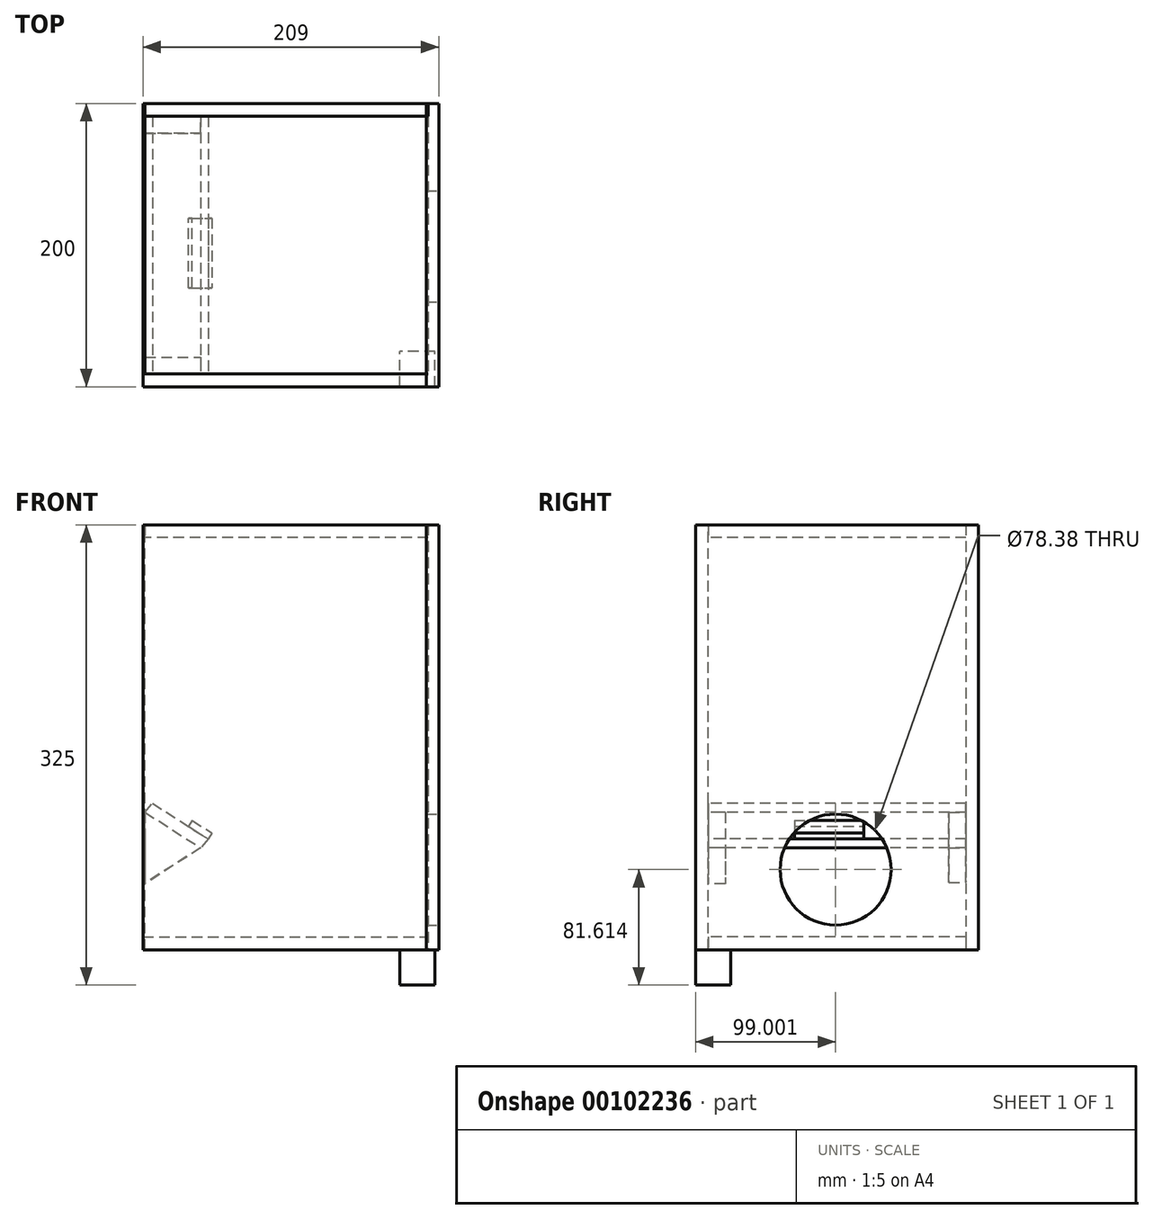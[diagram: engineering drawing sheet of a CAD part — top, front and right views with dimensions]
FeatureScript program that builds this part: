
annotation { "Feature Type Name" : "Feature", "Feature Type Description" : "" }
export const myFeature = defineFeature(function(context is Context, id is Id, definition is map)
    precondition{}
    {
        {
            var Q0;
            Q0=qCreatedBy(makeId("Front.planeOp"),FACE);
            var sketch = newSketch(context, id + "F0", { "sketchPlane" : qUnion([Q0])});
            skLineSegment(sketch, "E0.bottom", {"start": v(0, 0) * mm, "end": v(200, 0) * mm});
            skLineSegment(sketch, "E0.top", {"start": v(0, 300) * mm, "end": v(200, 300) * mm});
            skLineSegment(sketch, "E0.left", {"start": v(0, 0) * mm, "end": v(0, 300) * mm});
            skLineSegment(sketch, "E0.right", {"start": v(200, 0) * mm, "end": v(200, 300) * mm});
            skSolve(sketch);
        }
        {
            var Q0;
            Q0=makeQuery(id+"F0.imprint","IMPRINT",FACE,{"disambiguationData":[TD([[makeQuery(id+"F0.imprint","IMPRINT",EDGE,{"derivedFrom":sQuery(id+"F0.wireOp",EDGE,"E0.bottom")}),1.0]])]});
            extrude(context, id + "F1", {"entities" : qUnion([Q0]), "depth" : 9 * mm});
        }
        {
            var Q0;
            Q0=qCreatedBy(makeId("Front.planeOp"),FACE);
            var sketch = newSketch(context, id + "F2", { "sketchPlane" : qUnion([Q0])});
            skLineSegment(sketch, "E1.bottom", {"start": v(0, 0) * mm, "end": v(1.5, 0) * mm});
            skLineSegment(sketch, "E1.top", {"start": v(0, 300) * mm, "end": v(1.5, 300) * mm});
            skLineSegment(sketch, "E1.left", {"start": v(0, 0) * mm, "end": v(0, 300) * mm});
            skLineSegment(sketch, "E1.right", {"start": v(1.5, 0) * mm, "end": v(1.5, 300) * mm});
            skSolve(sketch);
        }
        {
            var Q0;
            Q0 = qSketchRegion(id + "F2", true);
            extrude(context, id + "F3", {"entities" : qUnion([Q0]), "oppositeDirection" : true, "depth" : 191 * mm});
        }
        {
            var Q0;
            Q0=makeQuery(id+"F0.imprint","IMPRINT",FACE,{"disambiguationData":[TD([[makeQuery(id+"F0.imprint","IMPRINT",EDGE,{"derivedFrom":sQuery(id+"F0.wireOp",EDGE,"E0.bottom")}),1.0]])]});
            var sketch = newSketch(context, id + "F4", { "sketchPlane" : qUnion([Q0])});
            skLineSegment(sketch, "E2", {"start": v(1.5, 97.07) * mm, "end": v(1.5, 46.7) * mm});
            skLineSegment(sketch, "E3", {"start": v(1.5, 97.07) * mm, "end": v(40.82, 71.89) * mm});
            skLineSegment(sketch, "E4", {"start": v(40.82, 71.89) * mm, "end": v(1.5, 46.7) * mm});
            skSolve(sketch);
        }
        {
            var Q0;
            Q0 = qSketchRegion(id + "F4", true);
            extrude(context, id + "F5", {"entities" : qUnion([Q0]), "oppositeDirection" : true, "depth" : 12 * mm});
        }
        {
            var Q0;
            Q0=makeQuery(id+"F0.imprint","IMPRINT",FACE,{"disambiguationData":[TD([[makeQuery(id+"F0.imprint","IMPRINT",EDGE,{"derivedFrom":sQuery(id+"F0.wireOp",EDGE,"E0.bottom")}),1.0]])]});
            var sketch = newSketch(context, id + "F6", { "sketchPlane" : qUnion([Q0])});
            skLineSegment(sketch, "E5", {"start": v(1.5, 97.07) * mm, "end": v(6.74, 103.42) * mm});
            skLineSegment(sketch, "E6", {"start": v(6.74, 103.42) * mm, "end": v(46.08, 78.24) * mm});
            skLineSegment(sketch, "E7", {"start": v(46.08, 78.24) * mm, "end": v(40.82, 71.89) * mm});
            skLineSegment(sketch, "E8", {"start": v(1.5, 97.07) * mm, "end": v(40.82, 71.89) * mm});
            skSolve(sketch);
        }
        {
            var Q0;
            Q0 = qSketchRegion(id + "F6", true);
            extrude(context, id + "F7", {"entities" : qUnion([Q0]), "oppositeDirection" : true, "depth" : 182 * mm});
        }
        {
            var Q0;
            Q0=makeQuery(id+"F7.opExtrude","CAP_FACE",FACE,{"disambiguationData":[OSD([sQuery(id+"F6.wireOp",EDGE,"E5"),sQuery(id+"F6.wireOp",EDGE,"E6"),sQuery(id+"F6.wireOp",EDGE,"E7"),sQuery(id+"F6.wireOp",EDGE,"E8")])],"isStart":false});
            var sketch = newSketch(context, id + "F8", { "sketchPlane" : qUnion([Q0])});
            skLineSegment(sketch, "E9", {"start": v(-40.82, 71.89) * mm, "end": v(-1.73, 47.36) * mm});
            skLineSegment(sketch, "E10", {"start": v(-1.73, 47.36) * mm, "end": v(-1.5, 97.07) * mm});
            skLineSegment(sketch, "E11", {"start": v(-1.5, 97.07) * mm, "end": v(-40.82, 71.89) * mm});
            skSolve(sketch);
        }
        {
            var Q0;
            Q0 = qSketchRegion(id + "F8", true);
            extrude(context, id + "F9", {"entities" : qUnion([Q0]), "oppositeDirection" : true, "depth" : 12 * mm});
        }
        {
            var Q0;
            Q0=makeQuery(id+"F7.opExtrude","SWEPT_FACE",FACE,{"disambiguationData":[OSD([sQuery(id+"F6.wireOp",EDGE,"E6")])]});
            var sketch = newSketch(context, id + "F10", { "sketchPlane" : qUnion([Q0])});
            skLineSegment(sketch, "E12.bottom", {"start": v(-19.9, 60.86) * mm, "end": v(-3.38, 60.86) * mm});
            skLineSegment(sketch, "E12.top", {"start": v(-19.9, 110) * mm, "end": v(-3.38, 110) * mm});
            skLineSegment(sketch, "E12.left", {"start": v(-19.9, 60.86) * mm, "end": v(-19.9, 110) * mm});
            skLineSegment(sketch, "E12.right", {"start": v(-3.38, 60.86) * mm, "end": v(-3.38, 110) * mm});
            skSolve(sketch);
        }
        {
            var Q0;
            Q0 = qSketchRegion(id + "F10", true);
            extrude(context, id + "F11", {"entities" : qUnion([Q0]), "depth" : 5 * mm});
        }
        {
            var Q0;
            Q0=makeQuery(id+"F0.imprint","IMPRINT",FACE,{"disambiguationData":[TD([[makeQuery(id+"F0.imprint","IMPRINT",EDGE,{"derivedFrom":sQuery(id+"F0.wireOp",EDGE,"E0.bottom")}),1.0]])]});
            var sketch = newSketch(context, id + "F12", { "sketchPlane" : qUnion([Q0])});
            skLineSegment(sketch, "E13.bottom", {"start": v(201.5, 300) * mm, "end": v(1.5, 300) * mm});
            skLineSegment(sketch, "E13.top", {"start": v(201.5, 291) * mm, "end": v(1.5, 291) * mm});
            skLineSegment(sketch, "E13.left", {"start": v(201.5, 300) * mm, "end": v(201.5, 291) * mm});
            skLineSegment(sketch, "E13.right", {"start": v(1.5, 300) * mm, "end": v(1.5, 291) * mm});
            skSolve(sketch);
        }
        {
            var Q0;
            Q0 = qSketchRegion(id + "F12", true);
            extrude(context, id + "F13", {"entities" : qUnion([Q0]), "oppositeDirection" : true, "depth" : 182 * mm});
        }
        {
            var Q0;
            Q0=makeQuery(id+"F0.imprint","IMPRINT",FACE,{"disambiguationData":[TD([[makeQuery(id+"F0.imprint","IMPRINT",EDGE,{"derivedFrom":sQuery(id+"F0.wireOp",EDGE,"E0.bottom")}),1.0]])]});
            var sketch = newSketch(context, id + "F14", { "sketchPlane" : qUnion([Q0])});
            skLineSegment(sketch, "E14.bottom", {"start": v(0, 9) * mm, "end": v(200, 9) * mm});
            skLineSegment(sketch, "E14.top", {"start": v(0, 0) * mm, "end": v(200, 0) * mm});
            skLineSegment(sketch, "E14.left", {"start": v(0, 9) * mm, "end": v(0, 0) * mm});
            skLineSegment(sketch, "E14.right", {"start": v(200, 9) * mm, "end": v(200, 0) * mm});
            skSolve(sketch);
        }
        {
            var Q0;
            Q0 = qSketchRegion(id + "F14", true);
            extrude(context, id + "F15", {"entities" : qUnion([Q0]), "oppositeDirection" : true, "depth" : 182 * mm});
        }
        {
            var Q0;
            Q0=makeQuery(id+"F13.opExtrude","CAP_FACE",FACE,{"disambiguationData":[OSD([sQuery(id+"F12.wireOp",EDGE,"E13.bottom"),sQuery(id+"F12.wireOp",EDGE,"E13.top"),sQuery(id+"F12.wireOp",EDGE,"E13.left"),sQuery(id+"F12.wireOp",EDGE,"E13.right")])],"isStart":false});
            var sketch = newSketch(context, id + "F16", { "sketchPlane" : qUnion([Q0])});
            skLineSegment(sketch, "E15.bottom", {"start": v(-201.5, 300) * mm, "end": v(0, 300) * mm});
            skLineSegment(sketch, "E15.top", {"start": v(-201.5, 0) * mm, "end": v(0, 0) * mm});
            skLineSegment(sketch, "E15.left", {"start": v(-201.5, 300) * mm, "end": v(-201.5, 0) * mm});
            skLineSegment(sketch, "E15.right", {"start": v(0, 300) * mm, "end": v(0, 0) * mm});
            skSolve(sketch);
        }
        {
            var Q0;
            Q0 = qSketchRegion(id + "F16", true);
            extrude(context, id + "F17", {"entities" : qUnion([Q0]), "depth" : 9 * mm});
        }
        {
            var Q0;
            Q0=makeQuery(id+"F1.opExtrude","SWEPT_FACE",FACE,{"disambiguationData":[OSD([sQuery(id+"F0.wireOp",EDGE,"E0.right")])]});
            var sketch = newSketch(context, id + "F18", { "sketchPlane" : qUnion([Q0])});
            skLineSegment(sketch, "E16.bottom", {"start": v(-9, 300) * mm, "end": v(190.98, 300) * mm});
            skLineSegment(sketch, "E16.top", {"start": v(-9, 0) * mm, "end": v(190.98, 0) * mm});
            skLineSegment(sketch, "E16.left", {"start": v(-9, 300) * mm, "end": v(-9, 0) * mm});
            skLineSegment(sketch, "E16.right", {"start": v(190.98, 300) * mm, "end": v(190.98, 0) * mm});
            skSolve(sketch);
        }
        {
            var Q0;
            Q0 = qSketchRegion(id + "F18", true);
            extrude(context, id + "F19", {"entities" : qUnion([Q0]), "depth" : 9 * mm});
        }
        {
            var Q0;
            Q0=makeQuery(id+"F19.opExtrude","CAP_FACE",FACE,{"disambiguationData":[OSD([sQuery(id+"F18.wireOp",EDGE,"E16.bottom"),sQuery(id+"F18.wireOp",EDGE,"E16.top"),sQuery(id+"F18.wireOp",EDGE,"E16.left"),sQuery(id+"F18.wireOp",EDGE,"E16.right")])],"isStart":false});
            var sketch = newSketch(context, id + "F20", { "sketchPlane" : qUnion([Q0])});
            skCircle(sketch, "E17", {"center": v(90, 56.61) * mm, "radius": 39.2 * mm});
            skSolve(sketch);
        }
        {
            var Q0;
            Q0 = qSketchRegion(id + "F20", true);
            extrude(context, id + "F21", {"entities" : qUnion([Q0]), "operationType" : NewBodyOperationType.REMOVE, "oppositeDirection" : true, "depth" : 30 * mm});
        }
        {
            var Q0;
            Q0=makeQuery(id+"F1.opExtrude","SWEPT_FACE",FACE,{"disambiguationData":[OSD([sQuery(id+"F0.wireOp",EDGE,"E0.bottom")])]});
            var sketch = newSketch(context, id + "F22", { "sketchPlane" : qUnion([Q0])});
            skLineSegment(sketch, "E18.bottom", {"start": v(206.28, 9) * mm, "end": v(181.28, 9) * mm});
            skLineSegment(sketch, "E18.top", {"start": v(206.28, -16) * mm, "end": v(181.28, -16) * mm});
            skLineSegment(sketch, "E18.left", {"start": v(206.28, 9) * mm, "end": v(206.28, -16) * mm});
            skLineSegment(sketch, "E18.right", {"start": v(181.28, 9) * mm, "end": v(181.28, -16) * mm});
            skSolve(sketch);
        }
        {
            var Q0;
            Q0 = qSketchRegion(id + "F22", true);
            extrude(context, id + "F23", {"entities" : qUnion([Q0]), "depth" : 25 * mm});
        }
    });
